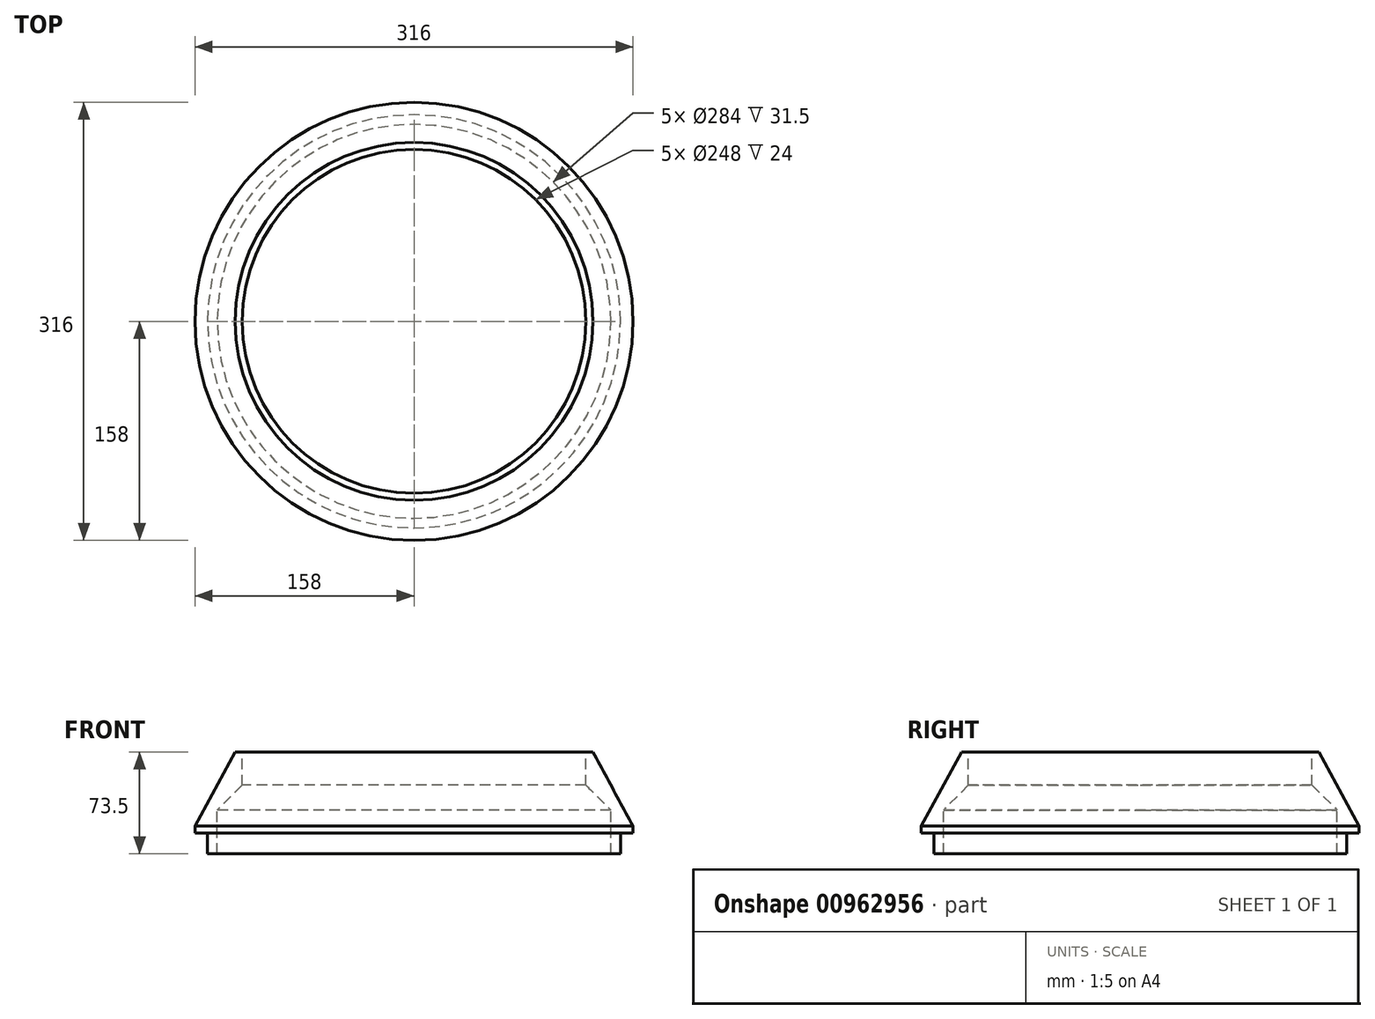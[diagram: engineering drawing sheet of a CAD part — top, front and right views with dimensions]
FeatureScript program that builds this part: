
annotation { "Feature Type Name" : "Feature", "Feature Type Description" : "" }
export const myFeature = defineFeature(function(context is Context, id is Id, definition is map)
    precondition{}
    {
        {
            var Q0;
            Q0=qCreatedBy(makeId("Front.planeOp"),FACE);
            var sketch = newSketch(context, id + "F0", { "sketchPlane" : qUnion([Q0])});
            skLineSegment(sketch, "E0", {"start": v(0, 179.59) * mm, "end": v(0, -190.64) * mm, "construction": true});
            skLineSegment(sketch, "E1", {"start": v(-149, 0) * mm, "end": v(-149, 15) * mm});
            skLineSegment(sketch, "E2", {"start": v(-149, 15) * mm, "end": v(-158, 15) * mm});
            skLineSegment(sketch, "E3", {"start": v(-158, 15) * mm, "end": v(-158, 20) * mm});
            skLineSegment(sketch, "E4", {"start": v(-149, 0) * mm, "end": v(-142, 0) * mm});
            skLineSegment(sketch, "E5", {"start": v(-142, 0) * mm, "end": v(-142, 31.5) * mm});
            skLineSegment(sketch, "E6", {"start": v(-124, 73.5) * mm, "end": v(-124, 49.5) * mm});
            skLineSegment(sketch, "E7", {"start": v(-142, 31.5) * mm, "end": v(-124, 49.5) * mm});
            skLineSegment(sketch, "E8", {"start": v(-124, 73.5) * mm, "end": v(-129, 73.5) * mm});
            skLineSegment(sketch, "E9", {"start": v(-129, 73.5) * mm, "end": v(-158, 20) * mm});
            skSolve(sketch);
        }
        {
            var Q0;
            Q0 = qSketchRegion(id + "F0", true);
            var Q1;
            Q1=sQuery(id+"F0.wireOp",EDGE,"E0");
            revolve(context, id + "F1", {"surfaceOperationType" : NewSurfaceOperationType.NEW, "entities" : qUnion([Q0]), "axis" : qUnion([Q1]), "revolveType" : RevolveType.FULL});
        }
    });
